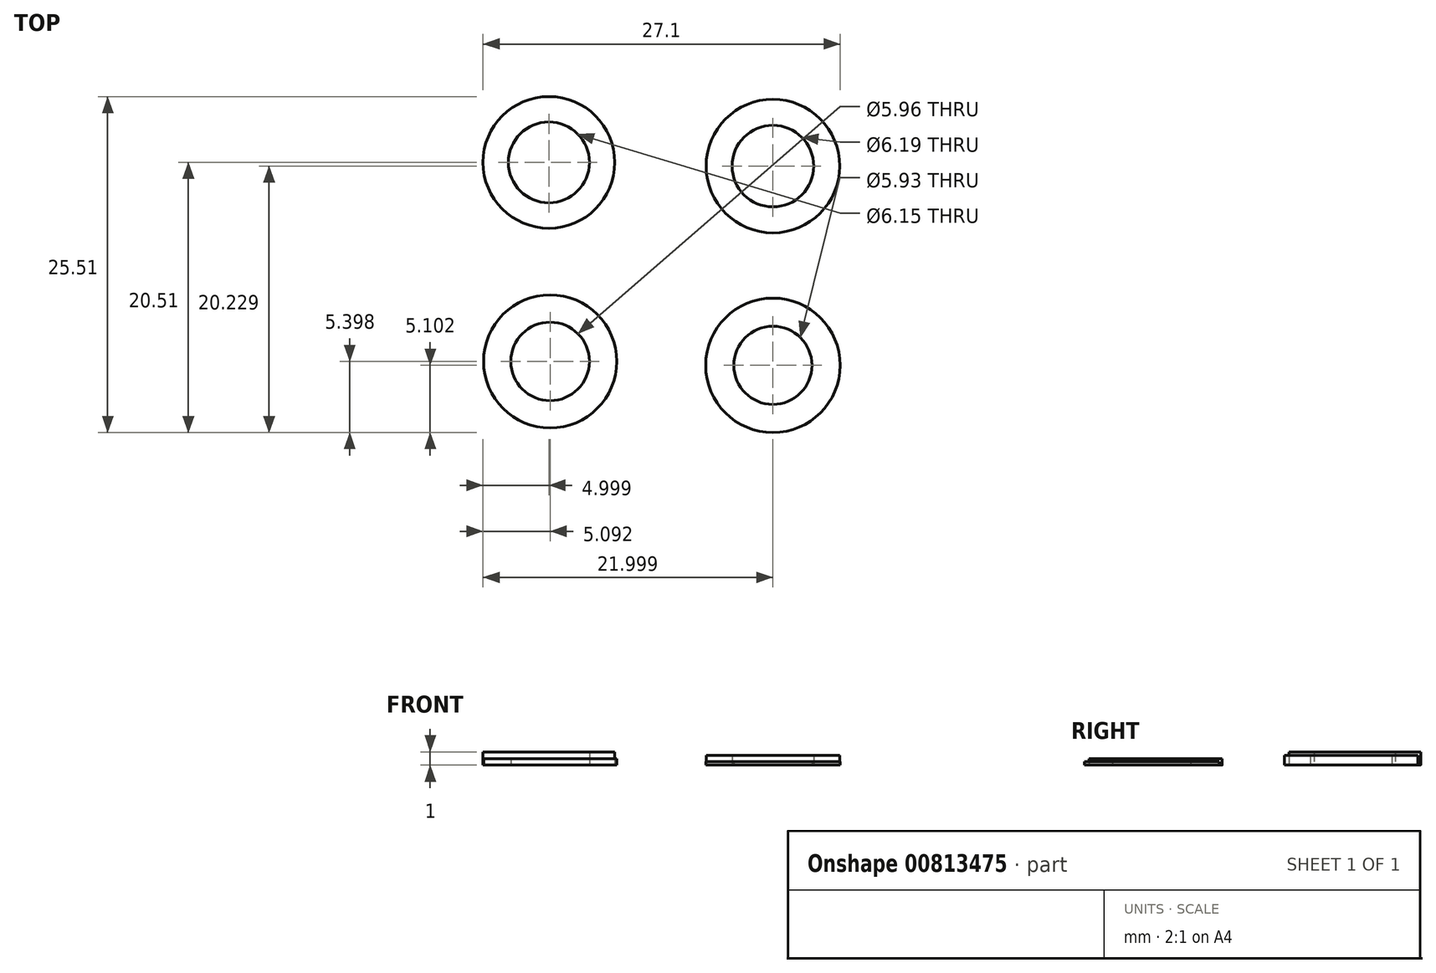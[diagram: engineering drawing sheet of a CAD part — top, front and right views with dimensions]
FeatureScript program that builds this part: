
annotation { "Feature Type Name" : "Feature", "Feature Type Description" : "" }
export const myFeature = defineFeature(function(context is Context, id is Id, definition is map)
    precondition{}
    {
        {
            var Q0;
            Q0=qCreatedBy(makeId("Top.planeOp"),FACE);
            var sketch = newSketch(context, id + "F0", { "sketchPlane" : qUnion([Q0])});
            skCircle(sketch, "E0", {"center": v(-43.62, 36.7) * mm, "radius": 5 * mm});
            skCircle(sketch, "E1", {"center": v(-43.62, 36.7) * mm, "radius": 3.07 * mm});
            skSolve(sketch);
        }
        {
            var Q0;
            Q0 = qSketchRegion(id + "F0", true);
            extrude(context, id + "F1", {"entities" : qUnion([Q0]), "depth" : 1 * mm, "offsetDistance" : 25 * mm});
        }
        {
            var Q0;
            Q0=qCreatedBy(makeId("Top.planeOp"),FACE);
            var sketch = newSketch(context, id + "F2", { "sketchPlane" : qUnion([Q0])});
            skCircle(sketch, "E2", {"center": v(-26.62, 36.4) * mm, "radius": 5.07 * mm});
            skCircle(sketch, "E3", {"center": v(-26.62, 36.4) * mm, "radius": 3.1 * mm});
            skSolve(sketch);
        }
        {
            var Q0;
            Q0 = qSketchRegion(id + "F2", true);
            extrude(context, id + "F3", {"entities" : qUnion([Q0]), "depth" : .75 * mm, "offsetDistance" : 25 * mm});
        }
        {
            var Q0;
            Q0=qCreatedBy(makeId("Top.planeOp"),FACE);
            var sketch = newSketch(context, id + "F4", { "sketchPlane" : qUnion([Q0])});
            skCircle(sketch, "E4", {"center": v(-43.53, 21.58) * mm, "radius": 5.05 * mm});
            skCircle(sketch, "E5", {"center": v(-43.53, 21.58) * mm, "radius": 2.98 * mm});
            skSolve(sketch);
        }
        {
            var Q0;
            Q0 = qSketchRegion(id + "F4", true);
            extrude(context, id + "F5", {"entities" : qUnion([Q0]), "depth" : .5 * mm, "offsetDistance" : 25 * mm});
        }
        {
            var Q0;
            Q0=qCreatedBy(makeId("Top.planeOp"),FACE);
            var sketch = newSketch(context, id + "F6", { "sketchPlane" : qUnion([Q0])});
            skCircle(sketch, "E6", {"center": v(-26.62, 21.28) * mm, "radius": 5.1 * mm});
            skCircle(sketch, "E7", {"center": v(-26.62, 21.28) * mm, "radius": 2.97 * mm});
            skSolve(sketch);
        }
        {
            var Q0;
            Q0 = qSketchRegion(id + "F6", true);
            extrude(context, id + "F7", {"entities" : qUnion([Q0]), "depth" : .25 * mm, "offsetDistance" : 25 * mm});
        }
    });
